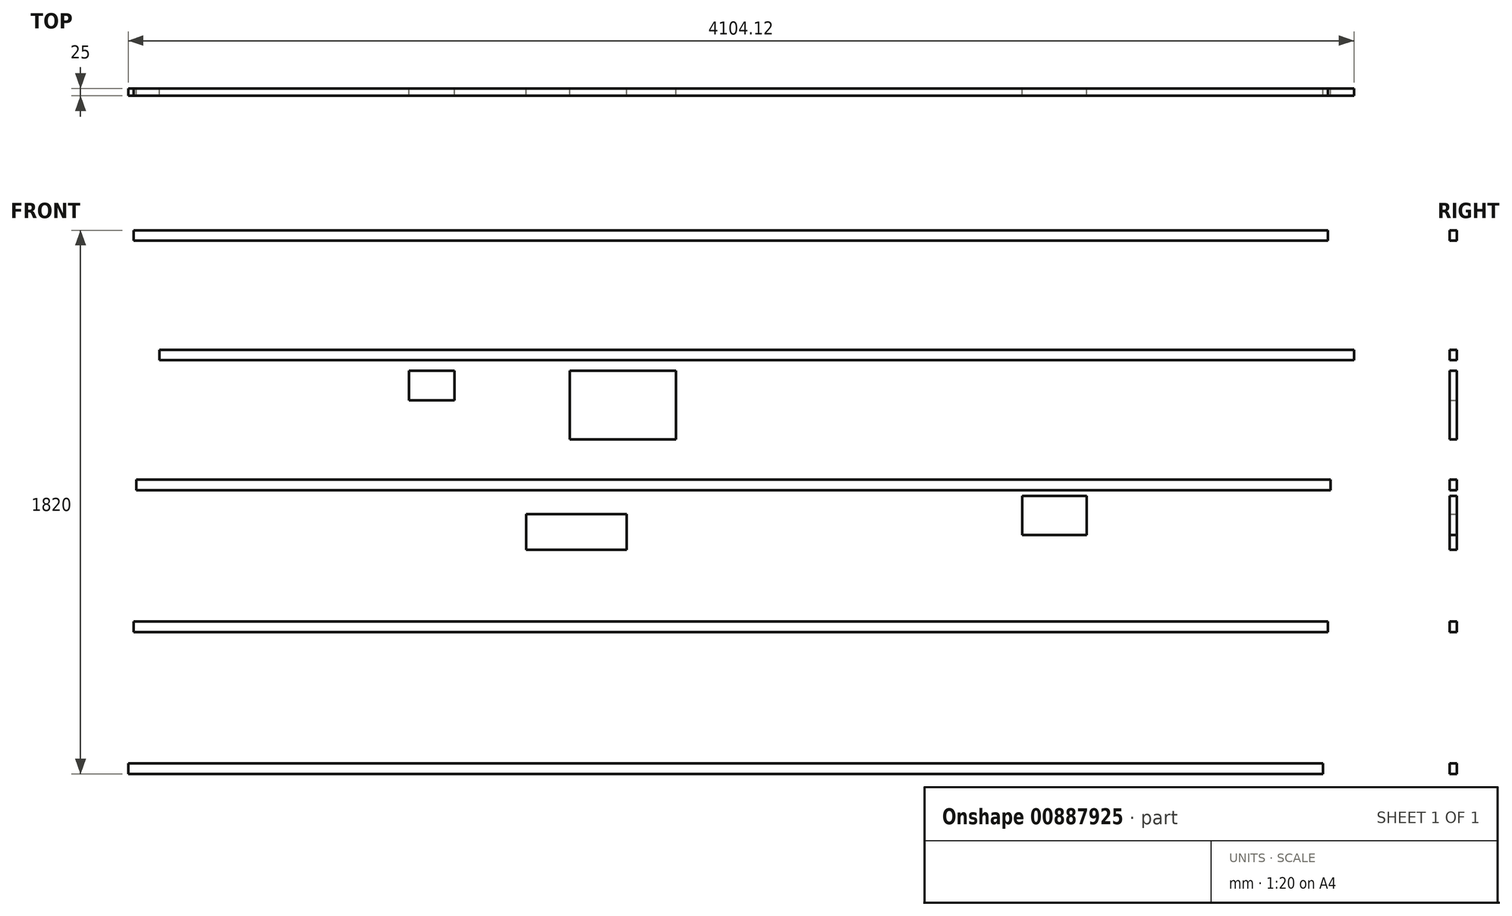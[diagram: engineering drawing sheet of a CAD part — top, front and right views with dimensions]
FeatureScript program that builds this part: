
annotation { "Feature Type Name" : "Feature", "Feature Type Description" : "" }
export const myFeature = defineFeature(function(context is Context, id is Id, definition is map)
    precondition{}
    {
        {
            var Q0;
            Q0=qCreatedBy(makeId("Front.planeOp"),FACE);
            var sketch = newSketch(context, id + "F0", { "sketchPlane" : qUnion([Q0])});
            skLineSegment(sketch, "E0.bottom", {"start": v(902.23, 1360) * mm, "end": v(1117.8, 1360) * mm});
            skLineSegment(sketch, "E0.top", {"start": v(902.23, 1230) * mm, "end": v(1117.8, 1230) * mm});
            skLineSegment(sketch, "E0.left", {"start": v(902.23, 1360) * mm, "end": v(902.23, 1230) * mm});
            skLineSegment(sketch, "E0.right", {"start": v(1117.8, 1360) * mm, "end": v(1117.8, 1230) * mm});
            skLineSegment(sketch, "E1.bottom", {"start": v(-758.9, 1300) * mm, "end": v(-422.87, 1300) * mm});
            skLineSegment(sketch, "E1.top", {"start": v(-758.9, 1180) * mm, "end": v(-422.87, 1180) * mm});
            skLineSegment(sketch, "E1.left", {"start": v(-758.9, 1300) * mm, "end": v(-758.9, 1180) * mm});
            skLineSegment(sketch, "E1.right", {"start": v(-422.87, 1300) * mm, "end": v(-422.87, 1180) * mm});
            skLineSegment(sketch, "E2.bottom", {"start": v(-1152, 1780) * mm, "end": v(-999.83, 1780) * mm});
            skLineSegment(sketch, "E2.top", {"start": v(-1152, 1680) * mm, "end": v(-999.83, 1680) * mm});
            skLineSegment(sketch, "E2.left", {"start": v(-1152, 1780) * mm, "end": v(-1152, 1680) * mm});
            skLineSegment(sketch, "E2.right", {"start": v(-999.83, 1780) * mm, "end": v(-999.83, 1680) * mm});
            skLineSegment(sketch, "E3.bottom", {"start": v(-613.08, 1780) * mm, "end": v(-258.03, 1780) * mm});
            skLineSegment(sketch, "E3.top", {"start": v(-613.08, 1550) * mm, "end": v(-258.03, 1550) * mm});
            skLineSegment(sketch, "E3.left", {"start": v(-613.08, 1780) * mm, "end": v(-613.08, 1550) * mm});
            skLineSegment(sketch, "E3.right", {"start": v(-258.03, 1780) * mm, "end": v(-258.03, 1550) * mm});
            skLineSegment(sketch, "E4.bottom", {"start": v(-2091.59, 465) * mm, "end": v(1908.41, 465) * mm});
            skLineSegment(sketch, "E4.top", {"start": v(-2091.59, 430) * mm, "end": v(1908.41, 430) * mm});
            skLineSegment(sketch, "E4.left", {"start": v(-2091.59, 465) * mm, "end": v(-2091.59, 430) * mm});
            skLineSegment(sketch, "E4.right", {"start": v(1908.41, 465) * mm, "end": v(1908.41, 430) * mm});
            skLineSegment(sketch, "E5.bottom", {"start": v(-2074.24, 940) * mm, "end": v(1925.76, 940) * mm});
            skLineSegment(sketch, "E5.top", {"start": v(-2074.24, 905) * mm, "end": v(1925.76, 905) * mm});
            skLineSegment(sketch, "E5.left", {"start": v(-2074.24, 940) * mm, "end": v(-2074.24, 905) * mm});
            skLineSegment(sketch, "E5.right", {"start": v(1925.76, 940) * mm, "end": v(1925.76, 905) * mm});
            skLineSegment(sketch, "E6.bottom", {"start": v(-2065.56, 1415) * mm, "end": v(1934.44, 1415) * mm});
            skLineSegment(sketch, "E6.top", {"start": v(-2065.56, 1380) * mm, "end": v(1934.44, 1380) * mm});
            skLineSegment(sketch, "E6.left", {"start": v(-2065.56, 1415) * mm, "end": v(-2065.56, 1380) * mm});
            skLineSegment(sketch, "E6.right", {"start": v(1934.44, 1415) * mm, "end": v(1934.44, 1380) * mm});
            skLineSegment(sketch, "E7.bottom", {"start": v(-1987.47, 1850) * mm, "end": v(2012.53, 1850) * mm});
            skLineSegment(sketch, "E7.top", {"start": v(-1987.47, 1815) * mm, "end": v(2012.53, 1815) * mm});
            skLineSegment(sketch, "E7.left", {"start": v(-1987.47, 1850) * mm, "end": v(-1987.47, 1815) * mm});
            skLineSegment(sketch, "E7.right", {"start": v(2012.53, 1850) * mm, "end": v(2012.53, 1815) * mm});
            skLineSegment(sketch, "E8.bottom", {"start": v(-2074.24, 2250) * mm, "end": v(1925.76, 2250) * mm});
            skLineSegment(sketch, "E8.top", {"start": v(-2074.24, 2215) * mm, "end": v(1925.76, 2215) * mm});
            skLineSegment(sketch, "E8.left", {"start": v(-2074.24, 2250) * mm, "end": v(-2074.24, 2215) * mm});
            skLineSegment(sketch, "E8.right", {"start": v(1925.76, 2250) * mm, "end": v(1925.76, 2215) * mm});
            skSolve(sketch);
        }
        {
            var Q0;
            Q0=makeQuery(id+"F0.imprint","IMPRINT",FACE,{"disambiguationData":[TD([[makeQuery(id+"F0.imprint","IMPRINT",EDGE,{"derivedFrom":sQuery(id+"F0.wireOp",EDGE,"E0.bottom")}),-1.0]])]});
            var Q1;
            Q1=makeQuery(id+"F0.imprint","IMPRINT",FACE,{"disambiguationData":[TD([[makeQuery(id+"F0.imprint","IMPRINT",EDGE,{"derivedFrom":sQuery(id+"F0.wireOp",EDGE,"E1.bottom")}),-1.0]])]});
            var Q2;
            Q2=makeQuery(id+"F0.imprint","IMPRINT",FACE,{"disambiguationData":[TD([[makeQuery(id+"F0.imprint","IMPRINT",EDGE,{"derivedFrom":sQuery(id+"F0.wireOp",EDGE,"E3.bottom")}),-1.0]])]});
            var Q3;
            Q3=makeQuery(id+"F0.imprint","IMPRINT",FACE,{"disambiguationData":[TD([[makeQuery(id+"F0.imprint","IMPRINT",EDGE,{"derivedFrom":sQuery(id+"F0.wireOp",EDGE,"E4.bottom")}),-1.0]])]});
            var Q4;
            Q4=makeQuery(id+"F0.imprint","IMPRINT",FACE,{"disambiguationData":[TD([[makeQuery(id+"F0.imprint","IMPRINT",EDGE,{"derivedFrom":sQuery(id+"F0.wireOp",EDGE,"E5.bottom")}),-1.0]])]});
            var Q5;
            Q5=makeQuery(id+"F0.imprint","IMPRINT",FACE,{"disambiguationData":[TD([[makeQuery(id+"F0.imprint","IMPRINT",EDGE,{"derivedFrom":sQuery(id+"F0.wireOp",EDGE,"E6.bottom")}),-1.0]])]});
            var Q6;
            Q6=makeQuery(id+"F0.imprint","IMPRINT",FACE,{"disambiguationData":[TD([[makeQuery(id+"F0.imprint","IMPRINT",EDGE,{"derivedFrom":sQuery(id+"F0.wireOp",EDGE,"E7.bottom")}),-1.0]])]});
            var Q7;
            Q7=makeQuery(id+"F0.imprint","IMPRINT",FACE,{"disambiguationData":[TD([[makeQuery(id+"F0.imprint","IMPRINT",EDGE,{"derivedFrom":sQuery(id+"F0.wireOp",EDGE,"E8.bottom")}),-1.0]])]});
            var Q8;
            Q8=makeQuery(id+"F0.imprint","IMPRINT",FACE,{"disambiguationData":[TD([[makeQuery(id+"F0.imprint","IMPRINT",EDGE,{"derivedFrom":sQuery(id+"F0.wireOp",EDGE,"E2.bottom")}),-1.0]])]});
            var Q9;
            Q9=sQuery(id+"F0.wireOp",EDGE,"E7.bottom");
            var Q10;
            Q10=sQuery(id+"F0.wireOp",EDGE,"E6.top");
            var Q11;
            Q11=sQuery(id+"F0.wireOp",EDGE,"E0.top");
            var Q12;
            Q12=sQuery(id+"F0.wireOp",EDGE,"E6.bottom");
            var Q13;
            Q13=sQuery(id+"F0.wireOp",EDGE,"E1.bottom");
            var Q14;
            Q14=sQuery(id+"F0.wireOp",EDGE,"E1.top");
            var Q15;
            Q15=sQuery(id+"F0.wireOp",EDGE,"E5.top");
            var Q16;
            Q16=sQuery(id+"F0.wireOp",EDGE,"E7.top");
            var Q17;
            Q17=sQuery(id+"F0.wireOp",EDGE,"E5.bottom");
            var Q18;
            Q18=sQuery(id+"F0.wireOp",EDGE,"E8.top");
            var Q19;
            Q19=sQuery(id+"F0.wireOp",EDGE,"E4.top");
            var Q20;
            Q20=sQuery(id+"F0.wireOp",EDGE,"E8.bottom");
            var Q21;
            Q21=sQuery(id+"F0.wireOp",EDGE,"E4.bottom");
            var Q22;
            Q22=sQuery(id+"F0.wireOp",EDGE,"E3.bottom");
            var Q23;
            Q23=sQuery(id+"F0.wireOp",EDGE,"E3.right");
            var Q24;
            Q24=sQuery(id+"F0.wireOp",EDGE,"E3.top");
            var Q25;
            Q25=sQuery(id+"F0.wireOp",EDGE,"E3.left");
            var Q26;
            Q26=sQuery(id+"F0.wireOp",EDGE,"E0.bottom");
            var Q27;
            Q27=sQuery(id+"F0.wireOp",EDGE,"E6.right");
            var Q28;
            Q28=sQuery(id+"F0.wireOp",EDGE,"E6.left");
            var Q29;
            Q29=sQuery(id+"F0.wireOp",EDGE,"E0.left");
            var Q30;
            Q30=sQuery(id+"F0.wireOp",EDGE,"E5.right");
            var Q31;
            Q31=sQuery(id+"F0.wireOp",EDGE,"E0.right");
            var Q32;
            Q32=sQuery(id+"F0.wireOp",EDGE,"E5.left");
            var Q33;
            Q33=sQuery(id+"F0.wireOp",EDGE,"E7.left");
            var Q34;
            Q34=sQuery(id+"F0.wireOp",EDGE,"E1.left");
            var Q35;
            Q35=sQuery(id+"F0.wireOp",EDGE,"E1.right");
            var Q36;
            Q36=sQuery(id+"F0.wireOp",EDGE,"E7.right");
            var Q37;
            Q37=sQuery(id+"F0.wireOp",EDGE,"E8.right");
            var Q38;
            Q38=sQuery(id+"F0.wireOp",EDGE,"E4.right");
            var Q39;
            Q39=sQuery(id+"F0.wireOp",EDGE,"E2.bottom");
            var Q40;
            Q40=sQuery(id+"F0.wireOp",EDGE,"E8.left");
            var Q41;
            Q41=sQuery(id+"F0.wireOp",EDGE,"E4.left");
            var Q42;
            Q42=sQuery(id+"F0.wireOp",EDGE,"E2.top");
            var Q43;
            Q43=sQuery(id+"F0.wireOp",EDGE,"E2.left");
            var Q44;
            Q44=sQuery(id+"F0.wireOp",EDGE,"E2.right");
            extrude(context, id + "F1", {"entities" : qUnion([Q0, Q1, Q2, Q3, Q4, Q5, Q6, Q7, Q8]), "surfaceEntities" : qUnion([Q9, Q10, Q11, Q12, Q13, Q14, Q15, Q16, Q17, Q18, Q19, Q20, Q21, Q22, Q23, Q24, Q25, Q26, Q27, Q28, Q29, Q30, Q31, Q32, Q33, Q34, Q35, Q36, Q37, Q38, Q39, Q40, Q41, Q42, Q43, Q44]), "depth" : 25 * mm, "offsetDistance" : 25 * mm});
        }
    });
